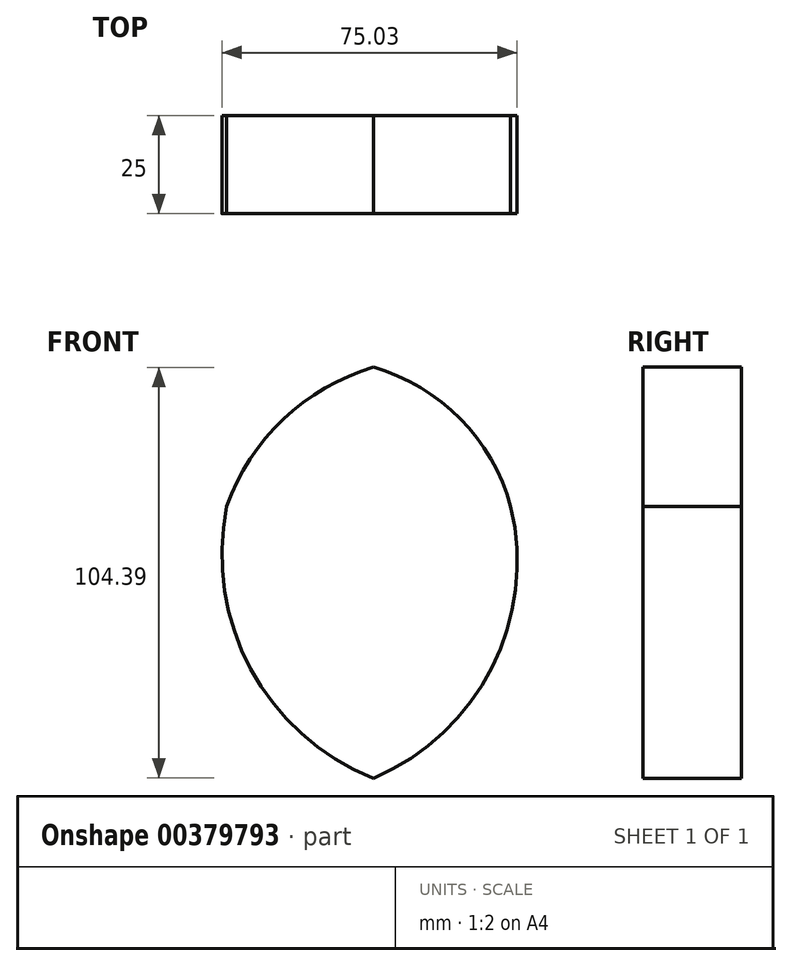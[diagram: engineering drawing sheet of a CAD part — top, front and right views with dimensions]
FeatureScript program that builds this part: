
annotation { "Feature Type Name" : "Feature", "Feature Type Description" : "" }
export const myFeature = defineFeature(function(context is Context, id is Id, definition is map)
    precondition{}
    {
        {
            var Q0;
            Q0=qCreatedBy(makeId("Front.planeOp"),FACE);
            var sketch = newSketch(context, id + "F0", { "sketchPlane" : qUnion([Q0])});
            skArc(sketch, "E0", {"start": v(0, 35.34) * mm, "mid": v(-22.87, 22.15) * mm, "end": v(-37.25, 0) * mm});
            skArc(sketch, "E1", {"start": v(34.89, 0) * mm, "mid": v(22.09, 22.25) * mm, "end": v(0, 35.34) * mm});
            skArc(sketch, "E2", {"start": v(0, -69.05) * mm, "mid": v(30.13, -40.94) * mm, "end": v(34.89, 0) * mm});
            skArc(sketch, "E3", {"start": v(-37.25, 0) * mm, "mid": v(-31.14, -41.28) * mm, "end": v(0, -69.05) * mm});
            skSolve(sketch);
        }
        {
            var Q0;
            Q0 = qSketchRegion(id + "F0", true);
            extrude(context, id + "F1", {"entities" : qUnion([Q0]), "depth" : 25 * mm, "offsetDistance" : 25 * mm});
        }
    });
